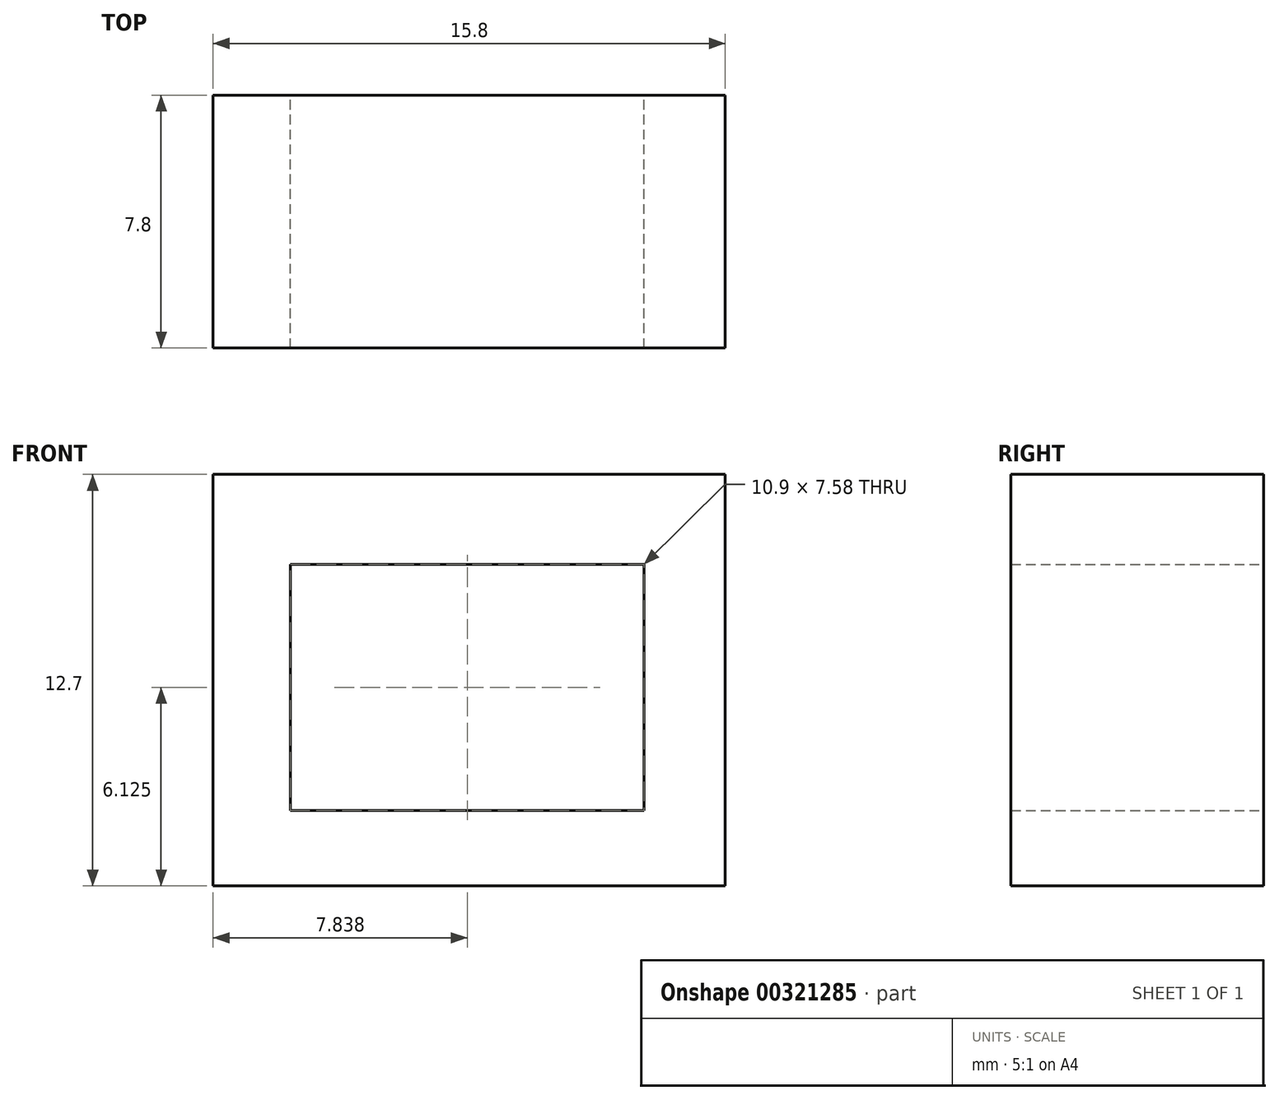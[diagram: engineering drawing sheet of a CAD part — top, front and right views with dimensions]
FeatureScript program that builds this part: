
annotation { "Feature Type Name" : "Feature", "Feature Type Description" : "" }
export const myFeature = defineFeature(function(context is Context, id is Id, definition is map)
    precondition{}
    {
        {
            var Q0;
            Q0=qCreatedBy(makeId("Front.planeOp"),FACE);
            var sketch = newSketch(context, id + "F0", { "sketchPlane" : qUnion([Q0])});
            skLineSegment(sketch, "E0.bottom", {"start": v(0, 0) * mm, "end": v(-15.8, 0) * mm});
            skLineSegment(sketch, "E0.top", {"start": v(0, 12.7) * mm, "end": v(-15.8, 12.7) * mm});
            skLineSegment(sketch, "E0.left", {"start": v(0, 0) * mm, "end": v(0, 12.7) * mm});
            skLineSegment(sketch, "E0.right", {"start": v(-15.8, 0) * mm, "end": v(-15.8, 12.7) * mm});
            skLineSegment(sketch, "E1.bottom", {"start": v(-2.51, 9.92) * mm, "end": v(-13.41, 9.92) * mm});
            skLineSegment(sketch, "E1.top", {"start": v(-2.51, 2.33) * mm, "end": v(-13.41, 2.33) * mm});
            skLineSegment(sketch, "E1.left", {"start": v(-2.51, 9.92) * mm, "end": v(-2.51, 2.33) * mm});
            skLineSegment(sketch, "E1.right", {"start": v(-13.41, 9.92) * mm, "end": v(-13.41, 2.33) * mm});
            skSolve(sketch);
        }
        {
            var Q0;
            Q0 = qSketchRegion(id + "F0", true);
            extrude(context, id + "F1", {"entities" : qUnion([Q0]), "depth" : 7.8 * mm});
        }
    });
